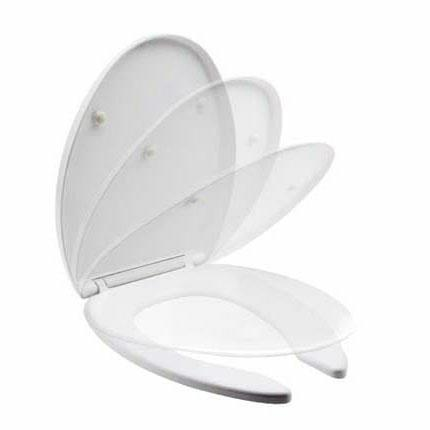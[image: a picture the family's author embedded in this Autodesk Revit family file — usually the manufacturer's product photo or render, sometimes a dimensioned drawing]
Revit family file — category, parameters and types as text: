
# Revit family: AT-4
name_source: partatom
category: Plumbing Fixtures
units: mm (PartAtom-declared; Revit-internal decimal feet)

## family parameters
Always vertical = Yes
Cut with Voids When Loaded = No
OmniClass Number = 23.45.00.00
OmniClass Title = Sanitary, Laundry, and Cleaning Equipment
Part Type = Normal
Room Calculation Point = No
Round Connector Dimension = Use Diameter
Shared = Yes
Work Plane-Based = No

## types (2) — shared parameters
Default Elevation = 0"
Manufacturer = HELVEX
Placement Height = 14.5"
Polypropylene = Polypropylene
Total Height = 2"
Total Length = 19"
Total Width = 14"
Type Comments = SANIVEX

## per-type parameters (varying)
| type | Data Sheet | Description | Features | Instructive | Type Image | URL |
| AT-2 | http://www.helvex.com.mx | Bearing Whit Standard Cap Seal | Premium Quality High Gloss; Antibacterial Protect; Adjustable Hinge | http://www.helvex.com.mx | <None> | http://www.helvex.com.mx |
| AT-4 | https://www.helvex.com.mx | Asiento para WC Elongado con Tapa Envolvente, Frente Abierto, Cierre Lento con Antibacterial | Acabado brillante con Protección
Antibacterial. | https://www.helvex.com.mx | AT-4.jpg | https://www.helvex.com.mx |

note: column(s) folded — value = type name in every type: Model

## geometry (parser evidence)
native form markers: Sweep x3
no freeform markers — native parametric forms only
